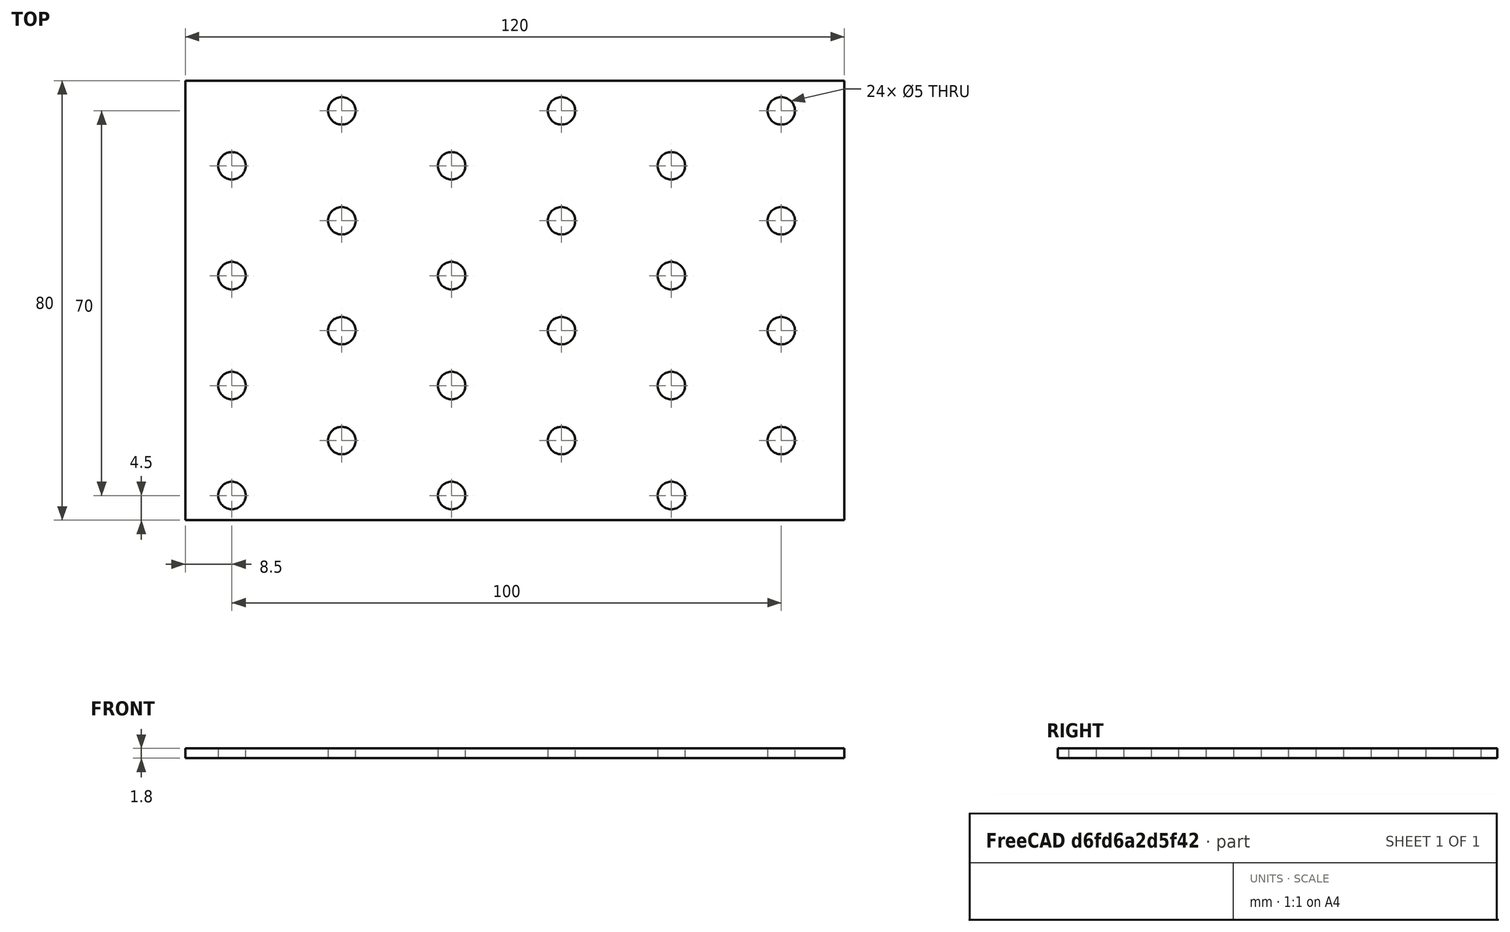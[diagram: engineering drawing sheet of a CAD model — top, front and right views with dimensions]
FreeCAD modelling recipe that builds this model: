
FCSTD DOCUMENT  (FreeCAD 0.19R24276 (Git))
Label: 80x120__1_8mm
License: All rights reserved
LicenseURL: http://en.wikipedia.org/wiki/All_rights_reserved
objects: Sketcher::SketchObject×1, PartDesign::Pad×1, PartDesign::Body×1
note: 4 computed .brp shape members not serialized (recipe doc carries the construction recipe); baked Part::Feature solids carry a one-line shape summary decoded from their .brp

FEATURE [Sketcher::SketchObject] Sketch
  FullyConstrained = false
  MapMode = 5
  Support = -> [XY_Plane]
  sketch-geometry (46):
    g0: LineSegment StartX=0 StartY=0 StartZ=0 EndX=120 EndY=0 EndZ=0
    g1: LineSegment StartX=120 StartY=0 StartZ=0 EndX=120 EndY=80 EndZ=0
    g2: LineSegment StartX=120 StartY=80 StartZ=0 EndX=0 EndY=80 EndZ=0
    g3: LineSegment StartX=0 StartY=80 StartZ=0 EndX=0 EndY=0 EndZ=0
    g4: LineSegment StartX=0 StartY=4.5 StartZ=0 EndX=120 EndY=4.5 EndZ=0
    g5: LineSegment StartX=0 StartY=24.5 StartZ=0 EndX=120 EndY=24.5 EndZ=0
    g6: LineSegment StartX=0 StartY=44.5 StartZ=0 EndX=120 EndY=44.5 EndZ=0
    g7: LineSegment StartX=0 StartY=64.5 StartZ=0 EndX=120 EndY=64.5 EndZ=0
    g8: LineSegment StartX=48.5 StartY=0 StartZ=0 EndX=48.5 EndY=4.5 EndZ=0
    g9: LineSegment StartX=68.5 StartY=0 StartZ=0 EndX=68.5 EndY=4.5 EndZ=0
    g10: LineSegment StartX=88.5 StartY=0 StartZ=0 EndX=88.5 EndY=4.5 EndZ=0
    g11: LineSegment StartX=108.5 StartY=0 StartZ=0 EndX=108.5 EndY=4.5 EndZ=0
    g12: LineSegment StartX=0 StartY=14.5 StartZ=0 EndX=120 EndY=14.5 EndZ=0
    g13: LineSegment StartX=0 StartY=34.5 StartZ=0 EndX=120 EndY=34.5 EndZ=0
    g14: LineSegment StartX=0 StartY=54.5 StartZ=0 EndX=120 EndY=54.5 EndZ=0
    g15: LineSegment StartX=0 StartY=74.5 StartZ=0 EndX=120 EndY=74.5 EndZ=0
    g16: LineSegment StartX=48.5 StartY=24.5 StartZ=0 EndX=48.5 EndY=80 EndZ=0
    g17: LineSegment StartX=68.5 StartY=14.5 StartZ=0 EndX=68.5 EndY=80 EndZ=0
    g18: LineSegment StartX=88.5 StartY=24.5 StartZ=0 EndX=88.5 EndY=80 EndZ=0
    g19: LineSegment StartX=108.5 StartY=14.5 StartZ=0 EndX=108.5 EndY=80 EndZ=0
    g20: Circle CenterX=8.5 CenterY=4.5 CenterZ=0 NormalX=0 NormalY=0 NormalZ=1 AngleXU=0 Radius=2.5
    g21: Circle CenterX=48.5 CenterY=4.5 CenterZ=0 NormalX=0 NormalY=0 NormalZ=1 AngleXU=0 Radius=2.5
    g22: Circle CenterX=88.5 CenterY=4.5 CenterZ=0 NormalX=0 NormalY=0 NormalZ=1 AngleXU=0 Radius=2.5
    g23: Circle CenterX=28.5 CenterY=14.5 CenterZ=0 NormalX=0 NormalY=0 NormalZ=1 AngleXU=0 Radius=2.5
    g24: Circle CenterX=108.5 CenterY=14.5 CenterZ=0 NormalX=0 NormalY=0 NormalZ=1 AngleXU=0 Radius=2.5
    g25: Circle CenterX=8.5 CenterY=24.5 CenterZ=0 NormalX=0 NormalY=0 NormalZ=1 AngleXU=0 Radius=2.5
    g26: Circle CenterX=48.5 CenterY=24.5 CenterZ=0 NormalX=0 NormalY=0 NormalZ=1 AngleXU=0 Radius=2.5
    g27: Circle CenterX=88.5 CenterY=24.5 CenterZ=0 NormalX=0 NormalY=0 NormalZ=1 AngleXU=0 Radius=2.5
    g28: Circle CenterX=8.5 CenterY=44.5 CenterZ=0 NormalX=0 NormalY=0 NormalZ=1 AngleXU=0 Radius=2.5
    g29: Circle CenterX=48.5 CenterY=44.5 CenterZ=0 NormalX=0 NormalY=0 NormalZ=1 AngleXU=0 Radius=2.5
    g30: Circle CenterX=88.5 CenterY=44.5 CenterZ=0 NormalX=0 NormalY=0 NormalZ=1 AngleXU=0 Radius=2.5
    g31: Circle CenterX=28.5 CenterY=54.5 CenterZ=0 NormalX=0 NormalY=0 NormalZ=1 AngleXU=0 Radius=2.5
    g32: Circle CenterX=68.5 CenterY=54.5 CenterZ=0 NormalX=0 NormalY=0 NormalZ=1 AngleXU=0 Radius=2.5
    g33: Circle CenterX=108.5 CenterY=54.5 CenterZ=0 NormalX=0 NormalY=0 NormalZ=1 AngleXU=0 Radius=2.5
    g34: Circle CenterX=88.5 CenterY=64.5 CenterZ=0 NormalX=0 NormalY=0 NormalZ=1 AngleXU=0 Radius=2.5
    g35: Circle CenterX=48.5 CenterY=64.5 CenterZ=0 NormalX=0 NormalY=0 NormalZ=1 AngleXU=0 Radius=2.5
    g36: Circle CenterX=8.5 CenterY=64.5 CenterZ=0 NormalX=0 NormalY=0 NormalZ=1 AngleXU=0 Radius=2.5
    g37: Circle CenterX=28.5 CenterY=34.5 CenterZ=0 NormalX=0 NormalY=0 NormalZ=1 AngleXU=0 Radius=2.5
    g38: Circle CenterX=68.5 CenterY=34.5 CenterZ=0 NormalX=0 NormalY=0 NormalZ=1 AngleXU=0 Radius=2.5
    g39: Circle CenterX=108.5 CenterY=34.5 CenterZ=0 NormalX=0 NormalY=0 NormalZ=1 AngleXU=0 Radius=2.5
    g40: Circle CenterX=28.5 CenterY=74.5 CenterZ=0 NormalX=0 NormalY=0 NormalZ=1 AngleXU=0 Radius=2.5
    g41: Circle CenterX=68.5 CenterY=74.5 CenterZ=0 NormalX=0 NormalY=0 NormalZ=1 AngleXU=0 Radius=2.5
    g42: Circle CenterX=108.5 CenterY=74.5 CenterZ=0 NormalX=0 NormalY=0 NormalZ=1 AngleXU=0 Radius=2.5
    g43: LineSegment StartX=28.5 StartY=74.5 StartZ=0 EndX=28.5 EndY=14.5 EndZ=0
    g44: LineSegment StartX=8.5 StartY=4.5 StartZ=0 EndX=8.5 EndY=24.5 EndZ=0
    g45: Circle CenterX=68.5 CenterY=14.5 CenterZ=0 NormalX=0 NormalY=0 NormalZ=1 AngleXU=0 Radius=2.5
  constraints (100):
    c: Coincident(g0,g1)
    c: Coincident(g1,g2)
    c: Coincident(g2,g3)
    c: Coincident(g3,g0)
    c: Horizontal(g0)
    c: Horizontal(g2)
    c: Vertical(g1)
    c: Vertical(g3)
    c: Coincident(g0,g-1)
    c: DistanceX(g0,g0) = 120
    c: DistanceY(g3,g3) = 80
    c: Horizontal(g4)
    c: PointOnObject(g4,g3)
    c: PointOnObject(g4,g1)
    c: Horizontal(g5)
    c: PointOnObject(g5,g3)
    c: PointOnObject(g5,g1)
    c: DistanceY(g4,g5) = 20
    c: Horizontal(g6)
    c: PointOnObject(g6,g1)
    c: PointOnObject(g6,g3)
    c: DistanceY(g5,g6) = 20
    c: Horizontal(g7)
    c: PointOnObject(g7,g1)
    c: PointOnObject(g7,g3)
    c: DistanceY(g6,g7) = 20
    c: Vertical(g8)
    c: Vertical(g9)
    c: Vertical(g10)
    c: Vertical(g11)
    c: PointOnObject(g8,g0)
    c: PointOnObject(g9,g0)
    c: PointOnObject(g10,g0)
    c: PointOnObject(g11,g0)
    c: PointOnObject(g19,g2)
    c: PointOnObject(g18,g2)
    c: PointOnObject(g17,g2)
    c: PointOnObject(g16,g2)
    c: DistanceX(g8,g9) = 20
    c: DistanceX(g9,g10) = 20
    c: DistanceX(g10,g11) = 20
    c: Horizontal(g12)
    c: Horizontal(g13)
    c: Horizontal(g14)
    c: Horizontal(g15)
    c: PointOnObject(g12,g3)
    c: PointOnObject(g13,g3)
    c: PointOnObject(g14,g3)
    c: PointOnObject(g15,g3)
    c: PointOnObject(g15,g1)
    c: PointOnObject(g14,g1)
    c: PointOnObject(g13,g1)
    c: PointOnObject(g12,g1)
    c: DistanceY(g0,g12) = 14.5
    c: DistanceY(g12,g13) = 20
    c: DistanceY(g13,g14) = 20
    c: DistanceY(g14,g15) = 20
    c: PointOnObject(g20,g4)
    c: PointOnObject(g23,g12)
    c: PointOnObject(g8,g4)
    c: Tangent(g8,g16)
    c: PointOnObject(g9,g4)
    c: PointOnObject(g17,g12)
    c: Tangent(g9,g17)
    c: PointOnObject(g10,g4)
    c: Tangent(g10,g18)
    c: PointOnObject(g11,g4)
    c: PointOnObject(g19,g12)
    c: Tangent(g11,g19)
    c: Coincident(g21,g8)
    c: Coincident(g22,g10)
    c: Coincident(g24,g19)
    c: Equal(g20,g23)
    c: Equal(g23,g21)
    c: Equal(g21,g22)
    c: Equal(g22,g24)
    c: Diameter(g23) = 5
    c: PointOnObject(g16,g5)
    c: PointOnObject(g18,g5)
    c: Equal(g26,g27)
    c: Equal(g36,g31)
    c: Equal(g31,g35)
    c: Equal(g35,g34)
    c: Equal(g34,g33)
    c: Diameter(g31) = 5
    c: Equal(g34,g32)
    c: Equal(g29,g30)
    c: Diameter(g37) = 5
    c: Diameter(g40) = 5
    c: Coincident(g43,g40)
    c: Coincident(g43,g23)
    c: Vertical(g43)
    c: DistanceX(g20,g23) = 20
    c: DistanceX(g0,g20) = 8.5
    c: DistanceY(g0,g4) = 4.5
    c: Coincident(g44,g20)
    c: Coincident(g44,g25)
    c: Vertical(g44)
    c: Coincident(g45,g17)
    c: Equal(g24,g45)
FEATURE [PartDesign::Pad] Pad
  Direction = (1,1,1)
  Length = 1.8
  Length2 = 100
  Profile = -> Sketch
  Type = 0
FEATURE [PartDesign::Body] Body
  Group = -> [Sketch,Pad]
  Origin = -> Origin
  Tip = -> Pad
